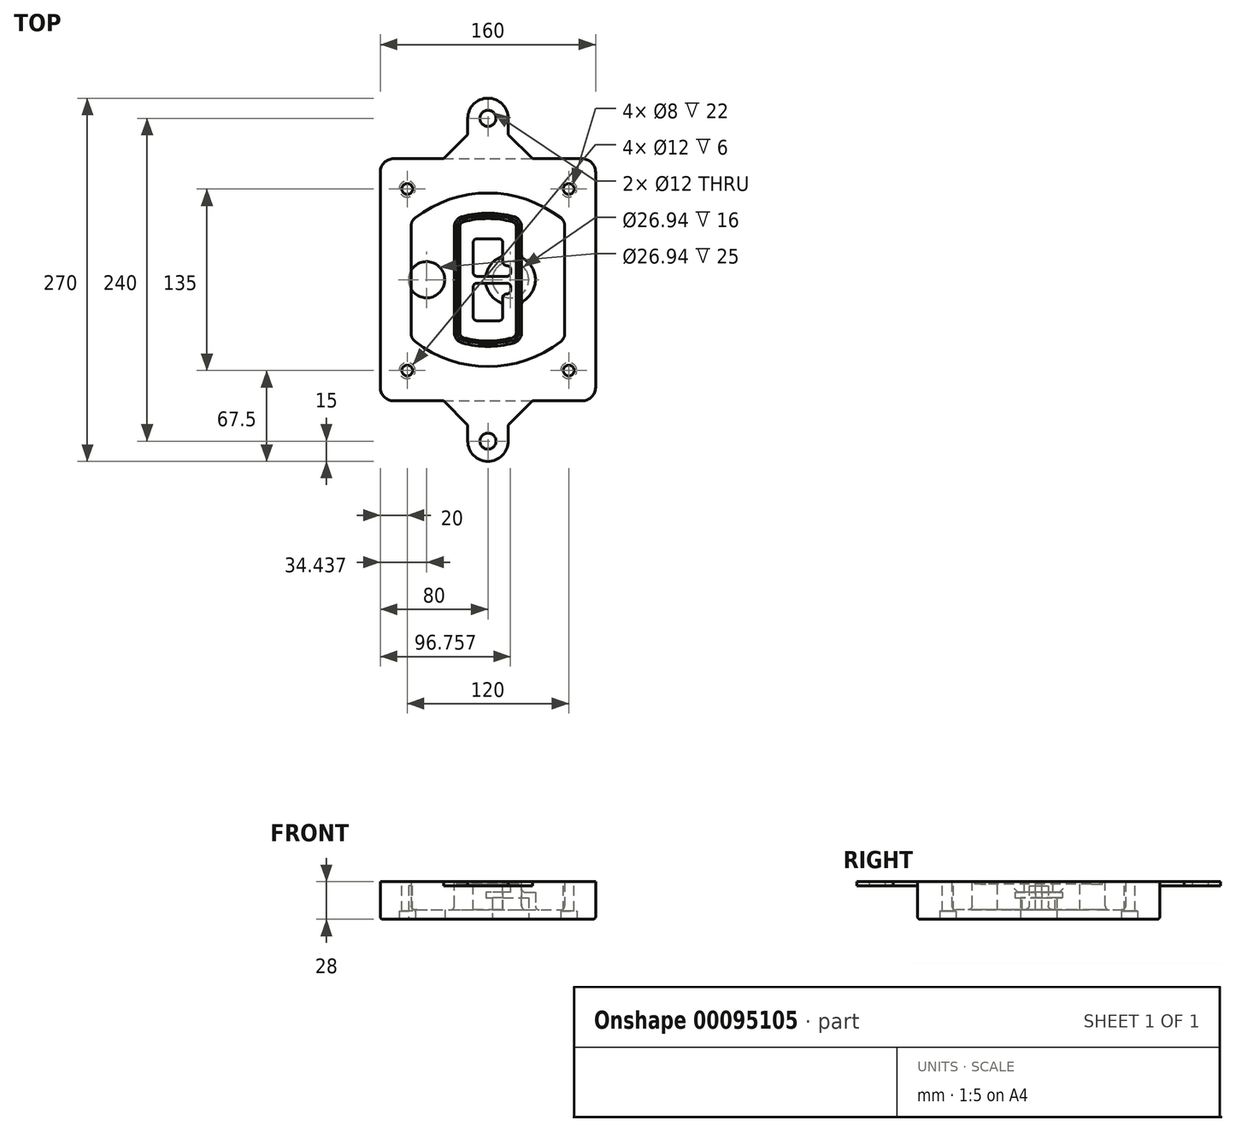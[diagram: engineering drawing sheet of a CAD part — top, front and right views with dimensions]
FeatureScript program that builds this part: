
annotation { "Feature Type Name" : "Feature", "Feature Type Description" : "" }
export const myFeature = defineFeature(function(context is Context, id is Id, definition is map)
    precondition{}
    {
        {
            var Q0;
            Q0=qCreatedBy(makeId("Top.planeOp"),FACE);
            var sketch = newSketch(context, id + "F0", { "sketchPlane" : qUnion([Q0])});
            skPoint(sketch, "E0.rect.middle", {"position": v(0, 0) * mm});
            skLineSegment(sketch, "E1.bottom", {"start": v(-70, -90) * mm, "end": v(70, -90) * mm});
            skLineSegment(sketch, "E1.top", {"start": v(-70, 90) * mm, "end": v(70, 90) * mm});
            skLineSegment(sketch, "E1.left", {"start": v(-80, -80) * mm, "end": v(-80, 80) * mm});
            skLineSegment(sketch, "E1.right", {"start": v(80, -80) * mm, "end": v(80, 80) * mm});
            skLineSegment(sketch, "E2", {"start": v(-80, 90) * mm, "end": v(80, -90) * mm, "construction": true});
            skLineSegment(sketch, "E3", {"start": v(80, 90) * mm, "end": v(-80, -90) * mm, "construction": true});
            skCircle(sketch, "E4", {"center": v(-60, 67.5) * mm, "radius": 4 * mm});
            skCircle(sketch, "E5", {"center": v(60, 67.5) * mm, "radius": 4 * mm});
            skCircle(sketch, "E6", {"center": v(60, -67.5) * mm, "radius": 4 * mm});
            skCircle(sketch, "E7", {"center": v(-60, -67.5) * mm, "radius": 4 * mm});
            skLineSegment(sketch, "E8", {"start": v(-60, 67.5) * mm, "end": v(60, 67.5) * mm, "construction": true});
            skLineSegment(sketch, "E9", {"start": v(60, 67.5) * mm, "end": v(60, -67.5) * mm, "construction": true});
            skLineSegment(sketch, "E10", {"start": v(60, -67.5) * mm, "end": v(-60, -67.5) * mm, "construction": true});
            skLineSegment(sketch, "E11", {"start": v(-60, -67.5) * mm, "end": v(-60, 67.5) * mm, "construction": true});
            skLineSegment(sketch, "E12", {"start": v(-60, 40.3) * mm, "end": v(-60, -40.3) * mm});
            skLineSegment(sketch, "E13", {"start": v(60, 40.3) * mm, "end": v(60, -40.3) * mm});
            skArc(sketch, "E14", {"start": v(56.15, 48.18) * mm, "mid": v(0, 67.5) * mm, "end": v(-56.15, 48.18) * mm});
            skArc(sketch, "E15", {"start": v(-56.15, -48.18) * mm, "mid": v(0, -67.5) * mm, "end": v(56.15, -48.18) * mm});
            skLineSegment(sketch, "E16", {"start": v(-60, 0) * mm, "end": v(60, 0) * mm, "construction": true});
            skPoint(sketch, "E17.visualSharp", {"position": v(-60, -45) * mm});
            skArc(sketch, "E17.filletArc", {"start": v(-60, -40.3) * mm, "mid": v(-58.99, -44.68) * mm, "end": v(-56.15, -48.18) * mm});
            skPoint(sketch, "E18.visualSharp", {"position": v(-60, 45) * mm});
            skArc(sketch, "E18.filletArc", {"start": v(-56.15, 48.18) * mm, "mid": v(-58.99, 44.68) * mm, "end": v(-60, 40.3) * mm});
            skPoint(sketch, "E19.visualSharp", {"position": v(60, 45) * mm});
            skArc(sketch, "E19.filletArc", {"start": v(60, 40.3) * mm, "mid": v(58.99, 44.68) * mm, "end": v(56.15, 48.18) * mm});
            skPoint(sketch, "E20.visualSharp", {"position": v(60, -45) * mm});
            skArc(sketch, "E20.filletArc", {"start": v(56.15, -48.18) * mm, "mid": v(58.99, -44.68) * mm, "end": v(60, -40.3) * mm});
            skPoint(sketch, "E21.visualSharp", {"position": v(-80, 90) * mm});
            skArc(sketch, "E21.filletArc", {"start": v(-70, 90) * mm, "mid": v(-77.07, 87.07) * mm, "end": v(-80, 80) * mm});
            skPoint(sketch, "E22.visualSharp", {"position": v(80, 90) * mm});
            skArc(sketch, "E22.filletArc", {"start": v(80, 80) * mm, "mid": v(77.07, 87.07) * mm, "end": v(70, 90) * mm});
            skPoint(sketch, "E23.visualSharp", {"position": v(80, -90) * mm});
            skArc(sketch, "E23.filletArc", {"start": v(70, -90) * mm, "mid": v(77.07, -87.07) * mm, "end": v(80, -80) * mm});
            skPoint(sketch, "E24.visualSharp", {"position": v(-80, -90) * mm});
            skArc(sketch, "E24.filletArc", {"start": v(-80, -80) * mm, "mid": v(-77.07, -87.07) * mm, "end": v(-70, -90) * mm});
            skArc(sketch, "E25.0", {"start": v(57, 40.3) * mm, "mid": v(56.3, 43.36) * mm, "end": v(54.3, 45.81) * mm});
            skLineSegment(sketch, "E25.1", {"start": v(57, 40.3) * mm, "end": v(57, -40.3) * mm});
            skArc(sketch, "E25.2", {"start": v(54.3, -45.81) * mm, "mid": v(56.3, -43.36) * mm, "end": v(57, -40.3) * mm});
            skArc(sketch, "E25.3", {"start": v(-54.3, -45.81) * mm, "mid": v(0, -64.5) * mm, "end": v(54.3, -45.81) * mm});
            skArc(sketch, "E25.4", {"start": v(-57, -40.3) * mm, "mid": v(-56.3, -43.36) * mm, "end": v(-54.3, -45.81) * mm});
            skArc(sketch, "E25.5", {"start": v(54.3, 45.81) * mm, "mid": v(0, 64.5) * mm, "end": v(-54.3, 45.81) * mm});
            skLineSegment(sketch, "E25.6", {"start": v(-57, 40.3) * mm, "end": v(-57, -40.3) * mm});
            skArc(sketch, "E25.7", {"start": v(-54.3, 45.81) * mm, "mid": v(-56.3, 43.36) * mm, "end": v(-57, 40.3) * mm});
            skArc(sketch, "E26.0", {"start": v(-58.62, 51.33) * mm, "mid": v(-62.58, 46.43) * mm, "end": v(-64, 40.3) * mm});
            skArc(sketch, "E26.1", {"start": v(58.62, 51.33) * mm, "mid": v(0, 71.5) * mm, "end": v(-58.62, 51.33) * mm});
            skArc(sketch, "E26.2", {"start": v(64, 40.3) * mm, "mid": v(62.58, 46.43) * mm, "end": v(58.62, 51.33) * mm});
            skLineSegment(sketch, "E26.3", {"start": v(64, 40.3) * mm, "end": v(64, -40.3) * mm});
            skArc(sketch, "E26.4", {"start": v(58.62, -51.33) * mm, "mid": v(62.58, -46.43) * mm, "end": v(64, -40.3) * mm});
            skLineSegment(sketch, "E26.5", {"start": v(-64, 40.3) * mm, "end": v(-64, -40.3) * mm});
            skArc(sketch, "E26.6", {"start": v(-58.62, -51.33) * mm, "mid": v(0, -71.5) * mm, "end": v(58.62, -51.33) * mm});
            skArc(sketch, "E26.7", {"start": v(-64, -40.3) * mm, "mid": v(-62.58, -46.43) * mm, "end": v(-58.62, -51.33) * mm});
            skSolve(sketch);
        }
        {
            var Q0;
            Q0=makeQuery(id+"F0.imprint","IMPRINT",FACE,{"disambiguationData":[TD([[makeQuery(id+"F0.imprint","IMPRINT",EDGE,{"derivedFrom":sQuery(id+"F0.wireOp",EDGE,"E1.bottom")}),1.0]])]});
            var Q1;
            Q1=makeQuery(id+"F0.imprint","IMPRINT",FACE,{"disambiguationData":[TD([[makeQuery(id+"F0.imprint","IMPRINT",EDGE,{"derivedFrom":sQuery(id+"F0.wireOp",EDGE,"E12")}),1.0]])]});
            var Q2;
            Q2=makeQuery(id+"F0.imprint","IMPRINT",FACE,{"disambiguationData":[TD([[makeQuery(id+"F0.imprint","IMPRINT",EDGE,{"derivedFrom":sQuery(id+"F0.wireOp",EDGE,"E25.0")}),1.0]])]});
            var Q3;
            Q3=makeQuery(id+"F0.imprint","IMPRINT",FACE,{"disambiguationData":[TD([[makeQuery(id+"F0.imprint","IMPRINT",EDGE,{"derivedFrom":sQuery(id+"F0.wireOp",EDGE,"E12")}),-1.0]])]});
            extrude(context, id + "F1", {"entities" : qUnion([Q0, Q1, Q2, Q3]), "oppositeDirection" : true, "depth" : 25 * mm});
        }
        {
            var Q0;
            Q0=makeQuery(id+"F0.imprint","IMPRINT",FACE,{"disambiguationData":[TD([[makeQuery(id+"F0.imprint","IMPRINT",EDGE,{"derivedFrom":sQuery(id+"F0.wireOp",EDGE,"E12")}),1.0]])]});
            extrude(context, id + "F2", {"entities" : qUnion([Q0]), "operationType" : NewBodyOperationType.ADD, "depth" : 3 * mm});
        }
        {
            var Q0;
            Q0=makeQuery(id+"F0.imprint","IMPRINT",FACE,{"disambiguationData":[TD([[makeQuery(id+"F0.imprint","IMPRINT",EDGE,{"derivedFrom":sQuery(id+"F0.wireOp",EDGE,"E25.0")}),1.0]])]});
            extrude(context, id + "F3", {"entities" : qUnion([Q0]), "operationType" : NewBodyOperationType.REMOVE, "oppositeDirection" : true, "depth" : 18 * mm});
        }
        {
            var Q0;
            Q0=makeQuery(id+"F2.opExtrude","CAP_FACE",FACE,{"disambiguationData":[OSD([sQuery(id+"F0.wireOp",EDGE,"E12"),sQuery(id+"F0.wireOp",EDGE,"E13"),sQuery(id+"F0.wireOp",EDGE,"E14"),sQuery(id+"F0.wireOp",EDGE,"E15"),sQuery(id+"F0.wireOp",EDGE,"E17.filletArc"),sQuery(id+"F0.wireOp",EDGE,"E18.filletArc"),sQuery(id+"F0.wireOp",EDGE,"E19.filletArc"),sQuery(id+"F0.wireOp",EDGE,"E20.filletArc"),sQuery(id+"F0.wireOp",EDGE,"E25.0"),sQuery(id+"F0.wireOp",EDGE,"E25.1"),sQuery(id+"F0.wireOp",EDGE,"E25.2"),sQuery(id+"F0.wireOp",EDGE,"E25.3"),sQuery(id+"F0.wireOp",EDGE,"E25.4"),sQuery(id+"F0.wireOp",EDGE,"E25.5"),sQuery(id+"F0.wireOp",EDGE,"E25.6"),sQuery(id+"F0.wireOp",EDGE,"E25.7")])],"isStart":false});
            var sketch = newSketch(context, id + "F4", { "sketchPlane" : qUnion([Q0])});
            skArc(sketch, "E27.0", {"start": v(-19.08, -46.97) * mm, "mid": v(0, -49.5) * mm, "end": v(19.08, -46.97) * mm});
            skArc(sketch, "E28.0", {"start": v(19.08, 46.97) * mm, "mid": v(0, 49.5) * mm, "end": v(-19.08, 46.97) * mm});
            skLineSegment(sketch, "E29", {"start": v(-25, 39.25) * mm, "end": v(-25, -39.25) * mm});
            skLineSegment(sketch, "E30", {"start": v(25, 39.25) * mm, "end": v(25, -39.25) * mm});
            skLineSegment(sketch, "E31", {"start": v(-25, 45.1) * mm, "end": v(25, 45.1) * mm, "construction": true});
            skLineSegment(sketch, "E32", {"start": v(-25, -45.1) * mm, "end": v(25, -45.1) * mm, "construction": true});
            skPoint(sketch, "E33.visualSharp", {"position": v(-25, 45.1) * mm});
            skArc(sketch, "E33.filletArc", {"start": v(-19.08, 46.97) * mm, "mid": v(-23.35, 44.11) * mm, "end": v(-25, 39.25) * mm});
            skPoint(sketch, "E34.visualSharp", {"position": v(25, 45.1) * mm});
            skArc(sketch, "E34.filletArc", {"start": v(25, 39.25) * mm, "mid": v(23.35, 44.11) * mm, "end": v(19.08, 46.97) * mm});
            skPoint(sketch, "E35.visualSharp", {"position": v(25, -45.1) * mm});
            skArc(sketch, "E35.filletArc", {"start": v(19.08, -46.97) * mm, "mid": v(23.35, -44.11) * mm, "end": v(25, -39.25) * mm});
            skPoint(sketch, "E36.visualSharp", {"position": v(-25, -45.1) * mm});
            skArc(sketch, "E36.filletArc", {"start": v(-25, -39.25) * mm, "mid": v(-23.35, -44.11) * mm, "end": v(-19.08, -46.97) * mm});
            skArc(sketch, "E37.0", {"start": v(54.3, 45.81) * mm, "mid": v(0, 64.5) * mm, "end": v(-54.3, 45.81) * mm});
            skArc(sketch, "E37.1", {"start": v(-54.3, 45.81) * mm, "mid": v(-56.3, 43.36) * mm, "end": v(-57, 40.3) * mm});
            skLineSegment(sketch, "E37.2", {"start": v(-57, 40.3) * mm, "end": v(-57, -40.3) * mm});
            skArc(sketch, "E37.3", {"start": v(-57, -40.3) * mm, "mid": v(-56.3, -43.36) * mm, "end": v(-54.3, -45.81) * mm});
            skArc(sketch, "E37.4", {"start": v(-54.3, -45.81) * mm, "mid": v(0, -64.5) * mm, "end": v(54.3, -45.81) * mm});
            skArc(sketch, "E37.5", {"start": v(54.3, -45.81) * mm, "mid": v(56.3, -43.36) * mm, "end": v(57, -40.3) * mm});
            skLineSegment(sketch, "E37.6", {"start": v(57, 40.3) * mm, "end": v(57, -40.3) * mm});
            skArc(sketch, "E37.7", {"start": v(57, 40.3) * mm, "mid": v(56.3, 43.36) * mm, "end": v(54.3, 45.81) * mm});
            skLineSegment(sketch, "E38.0", {"start": v(23, 39.25) * mm, "end": v(23, -39.25) * mm});
            skArc(sketch, "E38.1", {"start": v(18.56, -45.04) * mm, "mid": v(21.76, -42.9) * mm, "end": v(23, -39.25) * mm});
            skArc(sketch, "E38.2", {"start": v(-18.56, -45.04) * mm, "mid": v(0, -47.5) * mm, "end": v(18.56, -45.04) * mm});
            skArc(sketch, "E38.3", {"start": v(-23, -39.25) * mm, "mid": v(-21.76, -42.9) * mm, "end": v(-18.56, -45.04) * mm});
            skLineSegment(sketch, "E38.4", {"start": v(-23, 39.25) * mm, "end": v(-23, -39.25) * mm});
            skArc(sketch, "E38.5", {"start": v(23, 39.25) * mm, "mid": v(21.76, 42.9) * mm, "end": v(18.56, 45.04) * mm});
            skArc(sketch, "E38.6", {"start": v(-18.56, 45.04) * mm, "mid": v(-21.76, 42.9) * mm, "end": v(-23, 39.25) * mm});
            skArc(sketch, "E38.7", {"start": v(18.56, 45.04) * mm, "mid": v(0, 47.5) * mm, "end": v(-18.56, 45.04) * mm});
            skArc(sketch, "E39.0", {"start": v(21, 39.25) * mm, "mid": v(20.18, 41.68) * mm, "end": v(18.04, 43.1) * mm});
            skLineSegment(sketch, "E39.1", {"start": v(21, 39.25) * mm, "end": v(21, -39.25) * mm});
            skArc(sketch, "E39.2", {"start": v(18.04, -43.1) * mm, "mid": v(20.18, -41.68) * mm, "end": v(21, -39.25) * mm});
            skArc(sketch, "E39.3", {"start": v(-18.04, -43.1) * mm, "mid": v(0, -45.5) * mm, "end": v(18.04, -43.1) * mm});
            skArc(sketch, "E39.4", {"start": v(-21, -39.25) * mm, "mid": v(-20.18, -41.68) * mm, "end": v(-18.04, -43.1) * mm});
            skArc(sketch, "E39.5", {"start": v(18.04, 43.1) * mm, "mid": v(0, 45.5) * mm, "end": v(-18.04, 43.1) * mm});
            skLineSegment(sketch, "E39.6", {"start": v(-21, 39.25) * mm, "end": v(-21, -39.25) * mm});
            skArc(sketch, "E39.7", {"start": v(-18.04, 43.1) * mm, "mid": v(-20.18, 41.68) * mm, "end": v(-21, 39.25) * mm});
            skLineSegment(sketch, "E40", {"start": v(-25, 0) * mm, "end": v(25, 0) * mm, "construction": true});
            skLineSegment(sketch, "E41", {"start": v(-11, 5.5) * mm, "end": v(-11, 27.5) * mm});
            skLineSegment(sketch, "E42", {"start": v(-8, 30.5) * mm, "end": v(8, 30.5) * mm});
            skLineSegment(sketch, "E43", {"start": v(11, 27.5) * mm, "end": v(11, 13.5) * mm});
            skLineSegment(sketch, "E44", {"start": v(14, 10.5) * mm, "end": v(14, 10.5) * mm});
            skLineSegment(sketch, "E45", {"start": v(17, 7.5) * mm, "end": v(17, 5.5) * mm});
            skLineSegment(sketch, "E46", {"start": v(14, 2.5) * mm, "end": v(-8, 2.5) * mm});
            skPoint(sketch, "E47.visualSharp", {"position": v(-11, 30.5) * mm});
            skArc(sketch, "E47.filletArc", {"start": v(-8, 30.5) * mm, "mid": v(-10.12, 29.62) * mm, "end": v(-11, 27.5) * mm});
            skPoint(sketch, "E48.visualSharp", {"position": v(11, 30.5) * mm});
            skArc(sketch, "E48.filletArc", {"start": v(11, 27.5) * mm, "mid": v(10.12, 29.62) * mm, "end": v(8, 30.5) * mm});
            skPoint(sketch, "E49.visualSharp", {"position": v(11, 10.5) * mm});
            skArc(sketch, "E49.filletArc", {"start": v(11, 13.5) * mm, "mid": v(11.88, 11.38) * mm, "end": v(14, 10.5) * mm});
            skPoint(sketch, "E50.visualSharp", {"position": v(17, 10.5) * mm});
            skArc(sketch, "E50.filletArc", {"start": v(17, 7.5) * mm, "mid": v(16.12, 9.62) * mm, "end": v(14, 10.5) * mm});
            skPoint(sketch, "E51.visualSharp", {"position": v(17, 2.5) * mm});
            skArc(sketch, "E51.filletArc", {"start": v(14, 2.5) * mm, "mid": v(16.12, 3.38) * mm, "end": v(17, 5.5) * mm});
            skPoint(sketch, "E52.visualSharp", {"position": v(-11, 2.5) * mm});
            skArc(sketch, "E52.filletArc", {"start": v(-11, 5.5) * mm, "mid": v(-10.12, 3.38) * mm, "end": v(-8, 2.5) * mm});
            skLineSegment(sketch, "E53.0.MirrorCS", {"start": v(14, -2.5) * mm, "end": v(-8, -2.5) * mm});
            skArc(sketch, "E54.0.MirrorCS", {"start": v(-11, -5.5) * mm, "mid": v(-10.12, -3.38) * mm, "end": v(-8, -2.5) * mm});
            skLineSegment(sketch, "E55.0.MirrorCS", {"start": v(-11, -5.5) * mm, "end": v(-11, -27.5) * mm});
            skArc(sketch, "E56.0.MirrorCS", {"start": v(-8, -30.5) * mm, "mid": v(-10.12, -29.62) * mm, "end": v(-11, -27.5) * mm});
            skLineSegment(sketch, "E57.0.MirrorCS", {"start": v(-8, -30.5) * mm, "end": v(8, -30.5) * mm});
            skArc(sketch, "E58.0.MirrorCS", {"start": v(11, -27.5) * mm, "mid": v(10.12, -29.62) * mm, "end": v(8, -30.5) * mm});
            skLineSegment(sketch, "E59.0.MirrorCS", {"start": v(11, -27.5) * mm, "end": v(11, -13.5) * mm});
            skArc(sketch, "E60.0.MirrorCS", {"start": v(11, -13.5) * mm, "mid": v(11.88, -11.38) * mm, "end": v(14, -10.5) * mm});
            skArc(sketch, "E61.0.MirrorCS", {"start": v(17, -7.5) * mm, "mid": v(16.12, -9.62) * mm, "end": v(14, -10.5) * mm});
            skLineSegment(sketch, "E62.0.MirrorCS", {"start": v(17, -7.5) * mm, "end": v(17, -5.5) * mm});
            skArc(sketch, "E63.0.MirrorCS", {"start": v(14, -2.5) * mm, "mid": v(16.12, -3.38) * mm, "end": v(17, -5.5) * mm});
            skSolve(sketch);
        }
        {
            var Q0;
            Q0=makeQuery(id+"F4.imprint","IMPRINT",FACE,{"disambiguationData":[TD([[makeQuery(id+"F4.imprint","IMPRINT",EDGE,{"derivedFrom":sQuery(id+"F4.wireOp",EDGE,"E27.0")}),1.0]])]});
            var Q1;
            Q1=makeQuery(id+"F4.imprint","IMPRINT",FACE,{"disambiguationData":[TD([[makeQuery(id+"F4.imprint","IMPRINT",EDGE,{"derivedFrom":sQuery(id+"F4.wireOp",EDGE,"E38.0")}),-1.0]])]});
            var Q2;
            Q2=makeQuery(id+"F4.imprint","IMPRINT",FACE,{"disambiguationData":[TD([[makeQuery(id+"F4.imprint","IMPRINT",EDGE,{"derivedFrom":sQuery(id+"F4.wireOp",EDGE,"E39.0")}),1.0]])]});
            extrude(context, id + "F5", {"entities" : qUnion([Q0, Q1, Q2]), "operationType" : NewBodyOperationType.ADD, "endBound" : BoundingType.UP_TO_NEXT, "oppositeDirection" : true, "depth" : 25 * mm});
        }
        {
            var Q0;
            Q0=makeQuery(id+"F4.imprint","IMPRINT",FACE,{"disambiguationData":[TD([[makeQuery(id+"F4.imprint","IMPRINT",EDGE,{"derivedFrom":sQuery(id+"F4.wireOp",EDGE,"E38.0")}),-1.0]])]});
            extrude(context, id + "F6", {"entities" : qUnion([Q0]), "operationType" : NewBodyOperationType.REMOVE, "oppositeDirection" : true, "depth" : 2 * mm});
        }
        {
            var Q0;
            Q0=makeQuery(id+"F1.opExtrude","CAP_FACE",FACE,{"disambiguationData":[OSD([sQuery(id+"F0.wireOp",EDGE,"E1.bottom"),sQuery(id+"F0.wireOp",EDGE,"E1.top"),sQuery(id+"F0.wireOp",EDGE,"E1.left"),sQuery(id+"F0.wireOp",EDGE,"E1.right"),sQuery(id+"F0.wireOp",EDGE,"E4"),sQuery(id+"F0.wireOp",EDGE,"E5"),sQuery(id+"F0.wireOp",EDGE,"E6"),sQuery(id+"F0.wireOp",EDGE,"E7"),sQuery(id+"F0.wireOp",EDGE,"E21.filletArc"),sQuery(id+"F0.wireOp",EDGE,"E22.filletArc"),sQuery(id+"F0.wireOp",EDGE,"E23.filletArc"),sQuery(id+"F0.wireOp",EDGE,"E24.filletArc")])],"isStart":false});
            var sketch = newSketch(context, id + "F7", { "sketchPlane" : qUnion([Q0])});
            skCircle(sketch, "E64", {"center": v(16.76, 0) * mm, "radius": 13.47 * mm});
            skCircle(sketch, "E65", {"center": v(-45.56, 0) * mm, "radius": 13.47 * mm});
            skLineSegment(sketch, "E66", {"start": v(80, 0) * mm, "end": v(-80, 0) * mm});
            skCircle(sketch, "E67", {"center": v(16.76, 0) * mm, "radius": 18.47 * mm});
            skCircle(sketch, "E68", {"center": v(60, -67.5) * mm, "radius": 6 * mm});
            skCircle(sketch, "E69", {"center": v(-60, -67.5) * mm, "radius": 6 * mm});
            skCircle(sketch, "E70", {"center": v(-60, 67.5) * mm, "radius": 6 * mm});
            skCircle(sketch, "E71", {"center": v(60, 67.5) * mm, "radius": 6 * mm});
            skSolve(sketch);
        }
        {
            var Q0;
            {var subQ1=sQuery(id+"F7.wireOp",EDGE,"E66");var subQ4=sQuery(id+"F7.wireOp",EDGE,"E64");var subQ6=makeQuery(id+"F7.imprint","INTERSECT",VERTEX,{"disambiguationData":[OD(0.0)],"derivedFrom":[subQ4,subQ1]});Q0=makeQuery(id+"F7.imprint","IMPRINT",FACE,{"disambiguationData":[TD([[makeQuery(id+"F7.imprint","IMPRINT",EDGE,{"disambiguationData":[TD([[subQ6,-1.0]])],"derivedFrom":subQ4}),-1.0]])]});}
            var Q1;
            {var subQ0=sQuery(id+"F7.wireOp",EDGE,"E66");var subQ1=sQuery(id+"F7.wireOp",EDGE,"E64");var subQ3=makeQuery(id+"F7.imprint","INTERSECT",VERTEX,{"disambiguationData":[OD(0.0)],"derivedFrom":[subQ1,subQ0]});Q1=makeQuery(id+"F7.imprint","IMPRINT",FACE,{"disambiguationData":[TD([[makeQuery(id+"F7.imprint","IMPRINT",EDGE,{"disambiguationData":[TD([[subQ3,-1.0]])],"derivedFrom":subQ1}),1.0]])]});}
            var Q2;
            {var subQ0=sQuery(id+"F7.wireOp",EDGE,"E66");var subQ1=sQuery(id+"F7.wireOp",EDGE,"E64");var subQ3=makeQuery(id+"F7.imprint","INTERSECT",VERTEX,{"disambiguationData":[OD(0.0)],"derivedFrom":[subQ1,subQ0]});Q2=makeQuery(id+"F7.imprint","IMPRINT",FACE,{"disambiguationData":[TD([[makeQuery(id+"F7.imprint","IMPRINT",EDGE,{"disambiguationData":[TD([[subQ3,1.0]])],"derivedFrom":subQ1}),1.0]])]});}
            var Q3;
            {var subQ1=sQuery(id+"F7.wireOp",EDGE,"E66");var subQ4=sQuery(id+"F7.wireOp",EDGE,"E64");var subQ6=makeQuery(id+"F7.imprint","INTERSECT",VERTEX,{"disambiguationData":[OD(0.0)],"derivedFrom":[subQ4,subQ1]});Q3=makeQuery(id+"F7.imprint","IMPRINT",FACE,{"disambiguationData":[TD([[makeQuery(id+"F7.imprint","IMPRINT",EDGE,{"disambiguationData":[TD([[subQ6,1.0]])],"derivedFrom":subQ4}),-1.0]])]});}
            extrude(context, id + "F8", {"entities" : qUnion([Q0, Q1, Q2, Q3]), "operationType" : NewBodyOperationType.ADD, "oppositeDirection" : true, "depth" : 20 * mm});
        }
        {
            var Q0;
            {var subQ0=sQuery(id+"F7.wireOp",EDGE,"E66");var subQ1=sQuery(id+"F7.wireOp",EDGE,"E64");var subQ3=makeQuery(id+"F7.imprint","INTERSECT",VERTEX,{"disambiguationData":[OD(0.0)],"derivedFrom":[subQ1,subQ0]});Q0=makeQuery(id+"F7.imprint","IMPRINT",FACE,{"disambiguationData":[TD([[makeQuery(id+"F7.imprint","IMPRINT",EDGE,{"disambiguationData":[TD([[subQ3,-1.0]])],"derivedFrom":subQ1}),1.0]])]});}
            var Q1;
            {var subQ0=sQuery(id+"F7.wireOp",EDGE,"E66");var subQ1=sQuery(id+"F7.wireOp",EDGE,"E64");var subQ3=makeQuery(id+"F7.imprint","INTERSECT",VERTEX,{"disambiguationData":[OD(0.0)],"derivedFrom":[subQ1,subQ0]});Q1=makeQuery(id+"F7.imprint","IMPRINT",FACE,{"disambiguationData":[TD([[makeQuery(id+"F7.imprint","IMPRINT",EDGE,{"disambiguationData":[TD([[subQ3,1.0]])],"derivedFrom":subQ1}),1.0]])]});}
            extrude(context, id + "F9", {"entities" : qUnion([Q0, Q1]), "operationType" : NewBodyOperationType.REMOVE, "oppositeDirection" : true, "depth" : 16 * mm});
        }
        {
            var Q0;
            {var subQ0=sQuery(id+"F7.wireOp",EDGE,"E66");var subQ1=sQuery(id+"F7.wireOp",EDGE,"E65");var subQ3=makeQuery(id+"F7.imprint","INTERSECT",VERTEX,{"disambiguationData":[OD(0.0)],"derivedFrom":[subQ1,subQ0]});Q0=makeQuery(id+"F7.imprint","IMPRINT",FACE,{"disambiguationData":[TD([[makeQuery(id+"F7.imprint","IMPRINT",EDGE,{"disambiguationData":[TD([[subQ3,-1.0]])],"derivedFrom":subQ1}),1.0]])]});}
            var Q1;
            {var subQ0=sQuery(id+"F7.wireOp",EDGE,"E66");var subQ1=sQuery(id+"F7.wireOp",EDGE,"E65");var subQ3=makeQuery(id+"F7.imprint","INTERSECT",VERTEX,{"disambiguationData":[OD(0.0)],"derivedFrom":[subQ1,subQ0]});Q1=makeQuery(id+"F7.imprint","IMPRINT",FACE,{"disambiguationData":[TD([[makeQuery(id+"F7.imprint","IMPRINT",EDGE,{"disambiguationData":[TD([[subQ3,1.0]])],"derivedFrom":subQ1}),1.0]])]});}
            extrude(context, id + "F10", {"entities" : qUnion([Q0, Q1]), "operationType" : NewBodyOperationType.REMOVE, "oppositeDirection" : true, "depth" : 25 * mm});
        }
        {
            var Q0;
            Q0=makeQuery(id+"F7.imprint","IMPRINT",FACE,{"disambiguationData":[TD([[makeQuery(id+"F7.imprint","IMPRINT",EDGE,{"derivedFrom":sQuery(id+"F7.wireOp",EDGE,"E68")}),1.0]])]});
            var Q1;
            Q1=makeQuery(id+"F7.imprint","IMPRINT",FACE,{"disambiguationData":[TD([[makeQuery(id+"F7.imprint","IMPRINT",EDGE,{"derivedFrom":makeQuery(id+"F1.opExtrude","CAP_EDGE",EDGE,{"disambiguationData":[OSD([sQuery(id+"F0.wireOp",EDGE,"E5")])],"isStart":false})}),-1.0]])]});
            var Q2;
            Q2=makeQuery(id+"F7.imprint","IMPRINT",FACE,{"disambiguationData":[TD([[makeQuery(id+"F7.imprint","IMPRINT",EDGE,{"derivedFrom":sQuery(id+"F7.wireOp",EDGE,"E69")}),1.0]])]});
            var Q3;
            Q3=makeQuery(id+"F7.imprint","IMPRINT",FACE,{"disambiguationData":[TD([[makeQuery(id+"F7.imprint","IMPRINT",EDGE,{"derivedFrom":makeQuery(id+"F1.opExtrude","CAP_EDGE",EDGE,{"disambiguationData":[OSD([sQuery(id+"F0.wireOp",EDGE,"E4")])],"isStart":false})}),-1.0]])]});
            var Q4;
            Q4=makeQuery(id+"F7.imprint","IMPRINT",FACE,{"disambiguationData":[TD([[makeQuery(id+"F7.imprint","IMPRINT",EDGE,{"derivedFrom":sQuery(id+"F7.wireOp",EDGE,"E70")}),1.0]])]});
            var Q5;
            Q5=makeQuery(id+"F7.imprint","IMPRINT",FACE,{"disambiguationData":[TD([[makeQuery(id+"F7.imprint","IMPRINT",EDGE,{"derivedFrom":makeQuery(id+"F1.opExtrude","CAP_EDGE",EDGE,{"disambiguationData":[OSD([sQuery(id+"F0.wireOp",EDGE,"E7")])],"isStart":false})}),-1.0]])]});
            var Q6;
            Q6=makeQuery(id+"F7.imprint","IMPRINT",FACE,{"disambiguationData":[TD([[makeQuery(id+"F7.imprint","IMPRINT",EDGE,{"derivedFrom":sQuery(id+"F7.wireOp",EDGE,"E71")}),1.0]])]});
            var Q7;
            Q7=makeQuery(id+"F7.imprint","IMPRINT",FACE,{"disambiguationData":[TD([[makeQuery(id+"F7.imprint","IMPRINT",EDGE,{"derivedFrom":makeQuery(id+"F1.opExtrude","CAP_EDGE",EDGE,{"disambiguationData":[OSD([sQuery(id+"F0.wireOp",EDGE,"E6")])],"isStart":false})}),-1.0]])]});
            extrude(context, id + "F11", {"entities" : qUnion([Q0, Q1, Q2, Q3, Q4, Q5, Q6, Q7]), "operationType" : NewBodyOperationType.REMOVE, "oppositeDirection" : true, "depth" : 6 * mm});
        }
        {
            var Q0;
            Q0=makeQuery(id+"F9.boolean.opBoolean","COPY",FACE,{"derivedFrom":makeQuery(id+"F9.opExtrude","CAP_FACE",FACE,{"disambiguationData":[OSD([sQuery(id+"F7.wireOp",EDGE,"E64")])],"isStart":false})});
            var sketch = newSketch(context, id + "F12", { "sketchPlane" : qUnion([Q0])});
            skArc(sketch, "E72.0", {"start": v(11, 17.55) * mm, "mid": v(2.57, 11.82) * mm, "end": v(-1.54, 2.5) * mm});
            skArc(sketch, "E72.1", {"start": v(-1.54, -2.5) * mm, "mid": v(2.57, -11.82) * mm, "end": v(11, -17.55) * mm});
            skLineSegment(sketch, "E73", {"start": v(-1.54, -2.5) * mm, "end": v(14, -2.5) * mm});
            skLineSegment(sketch, "E74.0", {"start": v(14, 2.5) * mm, "end": v(-1.54, 2.5) * mm});
            skArc(sketch, "E74.1", {"start": v(14, 2.5) * mm, "mid": v(16.12, 3.38) * mm, "end": v(17, 5.5) * mm});
            skLineSegment(sketch, "E74.2", {"start": v(17, 7.5) * mm, "end": v(17, 5.5) * mm});
            skArc(sketch, "E74.3", {"start": v(17, 7.5) * mm, "mid": v(16.12, 9.62) * mm, "end": v(14, 10.5) * mm});
            skArc(sketch, "E74.4", {"start": v(11, 13.5) * mm, "mid": v(11.88, 11.38) * mm, "end": v(14, 10.5) * mm});
            skLineSegment(sketch, "E74.5", {"start": v(11, 17.55) * mm, "end": v(11, 13.5) * mm});
            skLineSegment(sketch, "E74.7", {"start": v(14, -2.5) * mm, "end": v(-1.54, -2.5) * mm});
            skArc(sketch, "E74.8", {"start": v(14, -2.5) * mm, "mid": v(16.12, -3.38) * mm, "end": v(17, -5.5) * mm});
            skLineSegment(sketch, "E74.9", {"start": v(17, -7.5) * mm, "end": v(17, -5.5) * mm});
            skArc(sketch, "E74.10", {"start": v(17, -7.5) * mm, "mid": v(16.12, -9.62) * mm, "end": v(14, -10.5) * mm});
            skArc(sketch, "E74.11", {"start": v(11, -13.5) * mm, "mid": v(11.88, -11.38) * mm, "end": v(14, -10.5) * mm});
            skLineSegment(sketch, "E74.12", {"start": v(11, -17.55) * mm, "end": v(11, -13.5) * mm});
            skPoint(sketch, "E75.orphan", {"position": v(11, -27.5) * mm});
            skPoint(sketch, "E76.orphan", {"position": v(-8, -2.5) * mm});
            skPoint(sketch, "E77.orphan", {"position": v(-8, 2.5) * mm});
            skPoint(sketch, "E78.orphan", {"position": v(11, 27.5) * mm});
            skSolve(sketch);
        }
        {
            var Q0;
            {var subQ7=sQuery(id+"F12.wireOp",EDGE,"E72.0");var subQ14=sQuery(id+"F12.wireOp",EDGE,"E72.1");var subQ16=sQuery(id+"F12.wireOp",EDGE,"E74.1");var subQ18=sQuery(id+"F12.wireOp",EDGE,"E74.8");Q0=qUnion([makeQuery(id+"F12.imprint","IMPRINT",FACE,{"disambiguationData":[TD([[makeQuery(id+"F12.imprint","IMPRINT",EDGE,{"derivedFrom":subQ7}),1.0]])]}),makeQuery(id+"F12.imprint","IMPRINT",FACE,{"disambiguationData":[TD([[makeQuery(id+"F12.imprint","IMPRINT",EDGE,{"derivedFrom":subQ14}),1.0]])]}),makeQuery(id+"F12.imprint","IMPRINT",FACE,{"disambiguationData":[TD([[makeQuery(id+"F12.imprint","IMPRINT",EDGE,{"derivedFrom":subQ16}),1.0]])]}),makeQuery(id+"F12.imprint","IMPRINT",FACE,{"disambiguationData":[TD([[makeQuery(id+"F12.imprint","IMPRINT",EDGE,{"derivedFrom":subQ18}),-1.0]])]})]);}
            var Q1;
            Q1=makeQuery(id+"F5.boolean.opBoolean","SPLIT",FACE,{"disambiguationData":[TD([makeQuery(id+"F5.opExtrude","SWEPT_FACE",FACE,{"disambiguationData":[OSD([sQuery(id+"F4.wireOp",EDGE,"E41")])]})])],"derivedFrom":makeQuery(id+"F3.boolean.opBoolean","COPY",FACE,{"derivedFrom":makeQuery(id+"F3.opExtrude","CAP_FACE",FACE,{"disambiguationData":[OSD([sQuery(id+"F0.wireOp",EDGE,"E25.0"),sQuery(id+"F0.wireOp",EDGE,"E25.1"),sQuery(id+"F0.wireOp",EDGE,"E25.2"),sQuery(id+"F0.wireOp",EDGE,"E25.3"),sQuery(id+"F0.wireOp",EDGE,"E25.4"),sQuery(id+"F0.wireOp",EDGE,"E25.5"),sQuery(id+"F0.wireOp",EDGE,"E25.6"),sQuery(id+"F0.wireOp",EDGE,"E25.7")])],"isStart":false})})});
            extrude(context, id + "F13", {"entities" : qUnion([Q0]), "operationType" : NewBodyOperationType.REMOVE, "endBound" : BoundingType.UP_TO_SURFACE, "endBoundEntityFace" : qUnion([Q1]), "depth" : 25 * mm});
        }
        {
            var Q0;
            Q0=makeQuery(id+"F3.boolean.opBoolean","COPY",EDGE,{"derivedFrom":makeQuery(id+"F3.opExtrude","CAP_EDGE",EDGE,{"disambiguationData":[OSD([sQuery(id+"F0.wireOp",EDGE,"E25.6")])],"isStart":false})});
            var Q1;
            Q1=makeQuery(id+"F8.boolean.opBoolean","INTERSECT",EDGE,{"derivedFrom":[makeQuery(id+"F5.opExtrude","SWEPT_FACE",FACE,{"disambiguationData":[OSD([sQuery(id+"F4.wireOp",EDGE,"E30")])]}),makeQuery(id+"F8.opExtrude","CAP_FACE",FACE,{"disambiguationData":[OSD([sQuery(id+"F7.wireOp",EDGE,"E67")])],"isStart":false})]});
            var Q2;
            Q2=makeQuery(id+"F8.boolean.opBoolean","INTERSECT",EDGE,{"disambiguationData":[OD(1.0)],"derivedFrom":[makeQuery(id+"F5.opExtrude","SWEPT_FACE",FACE,{"disambiguationData":[OSD([sQuery(id+"F4.wireOp",EDGE,"E30")])]}),makeQuery(id+"F8.opExtrude","SWEPT_FACE",FACE,{"disambiguationData":[OSD([sQuery(id+"F7.wireOp",EDGE,"E67")])]})]});
            var Q3;
            {var subQ0=sQuery(id+"F4.wireOp",EDGE,"E30");Q3=makeQuery(id+"F8.boolean.opBoolean","SPLIT",EDGE,{"disambiguationData":[TD([makeQuery(id+"F5.opExtrude","SWEPT_FACE",FACE,{"disambiguationData":[OSD([sQuery(id+"F4.wireOp",EDGE,"E35.filletArc")])]})])],"derivedFrom":makeQuery(id+"F5.opExtrude","CAP_EDGE",EDGE,{"disambiguationData":[OSD([subQ0])],"isStart":false})});}
            var Q4;
            {var subQ0=sQuery(id+"F0.wireOp",EDGE,"E25.7");var subQ1=sQuery(id+"F0.wireOp",EDGE,"E25.1");var subQ2=sQuery(id+"F0.wireOp",EDGE,"E25.6");var subQ3=sQuery(id+"F0.wireOp",EDGE,"E25.5");var subQ4=sQuery(id+"F0.wireOp",EDGE,"E25.4");var subQ5=sQuery(id+"F0.wireOp",EDGE,"E25.0");var subQ6=sQuery(id+"F0.wireOp",EDGE,"E25.2");var subQ7=sQuery(id+"F0.wireOp",EDGE,"E25.3");Q4=makeQuery(id+"F8.boolean.opBoolean","INTERSECT",EDGE,{"derivedFrom":[makeQuery(id+"F5.boolean.opBoolean","SPLIT",FACE,{"disambiguationData":[TD([makeQuery(id+"F2.opExtrude","SWEPT_FACE",FACE,{"disambiguationData":[OSD([subQ5])]})])],"derivedFrom":makeQuery(id+"F3.boolean.opBoolean","COPY",FACE,{"derivedFrom":makeQuery(id+"F3.opExtrude","CAP_FACE",FACE,{"disambiguationData":[OSD([subQ5,subQ1,subQ6,subQ7,subQ4,subQ3,subQ2,subQ0])],"isStart":false})})}),makeQuery(id+"F8.opExtrude","SWEPT_FACE",FACE,{"disambiguationData":[OSD([sQuery(id+"F7.wireOp",EDGE,"E67")])]})]});}
            var Q5;
            Q5=makeQuery(id+"F8.boolean.opBoolean","INTERSECT",EDGE,{"disambiguationData":[OD(0.0)],"derivedFrom":[makeQuery(id+"F5.opExtrude","SWEPT_FACE",FACE,{"disambiguationData":[OSD([sQuery(id+"F4.wireOp",EDGE,"E30")])]}),makeQuery(id+"F8.opExtrude","SWEPT_FACE",FACE,{"disambiguationData":[OSD([sQuery(id+"F7.wireOp",EDGE,"E67")])]})]});
            fillet(context, id + "F14", {"entities" : qUnion([Q0, Q1, Q2, Q3, Q4, Q5]), "radius" : 3 * mm, "tangentPropagation" : true, "allowEdgeOverflow" : false});
        }
        {
            var Q0;
            Q0=makeQuery(id+"F1.opExtrude","CAP_EDGE",EDGE,{"disambiguationData":[OSD([sQuery(id+"F0.wireOp",EDGE,"E1.bottom")])],"isStart":false});
            fillet(context, id + "F15", {"entities" : qUnion([Q0]), "radius" : 2 * mm, "tangentPropagation" : true, "allowEdgeOverflow" : false});
        }
        {
            var Q0;
            {var subQ0=sQuery(id+"F0.wireOp",EDGE,"E22.filletArc");var subQ1=sQuery(id+"F0.wireOp",EDGE,"E7");var subQ2=sQuery(id+"F0.wireOp",EDGE,"E6");var subQ3=sQuery(id+"F0.wireOp",EDGE,"E5");var subQ4=sQuery(id+"F0.wireOp",EDGE,"E4");var subQ5=sQuery(id+"F0.wireOp",EDGE,"E1.bottom");var subQ6=sQuery(id+"F0.wireOp",EDGE,"E21.filletArc");var subQ7=sQuery(id+"F0.wireOp",EDGE,"E1.top");var subQ8=sQuery(id+"F0.wireOp",EDGE,"E1.left");var subQ9=sQuery(id+"F0.wireOp",EDGE,"E1.right");var subQ10=sQuery(id+"F0.wireOp",EDGE,"E23.filletArc");var subQ11=sQuery(id+"F0.wireOp",EDGE,"E24.filletArc");Q0=makeQuery(id+"F2.boolean.opBoolean","SPLIT",FACE,{"disambiguationData":[TD([makeQuery(id+"F1.opExtrude","SWEPT_FACE",FACE,{"disambiguationData":[OSD([subQ5])]})])],"derivedFrom":makeQuery(id+"F1.opExtrude","CAP_FACE",FACE,{"disambiguationData":[OSD([subQ5,subQ7,subQ8,subQ9,subQ4,subQ3,subQ2,subQ1,subQ6,subQ0,subQ10,subQ11])],"isStart":true})});}
            var sketch = newSketch(context, id + "F16", { "sketchPlane" : qUnion([Q0])});
            skLineSegment(sketch, "E79", {"start": v(-33, 90) * mm, "end": v(-15, 108) * mm});
            skLineSegment(sketch, "E80", {"start": v(-15, 108) * mm, "end": v(-15, 120) * mm});
            skLineSegment(sketch, "E81", {"start": v(0, 90) * mm, "end": v(0, 120) * mm, "construction": true});
            skArc(sketch, "E82", {"start": v(-15, 120) * mm, "mid": v(0, 135) * mm, "end": v(15, 120) * mm});
            skLineSegment(sketch, "E83", {"start": v(15, 120) * mm, "end": v(15, 108) * mm});
            skLineSegment(sketch, "E84", {"start": v(15, 108) * mm, "end": v(33, 90) * mm});
            skCircle(sketch, "E85", {"center": v(0, 120) * mm, "radius": 6 * mm});
            skLineSegment(sketch, "E86", {"start": v(-80, 0) * mm, "end": v(80, 0) * mm, "construction": true});
            skLineSegment(sketch, "E87.MirrorCS", {"start": v(-33, -90) * mm, "end": v(-15, -108) * mm});
            skLineSegment(sketch, "E88.MirrorCS", {"start": v(15, -108) * mm, "end": v(33, -90) * mm});
            skLineSegment(sketch, "E89.MirrorCS", {"start": v(0, -90) * mm, "end": v(0, -120) * mm, "construction": true});
            skLineSegment(sketch, "E90.MirrorCS", {"start": v(15, -120) * mm, "end": v(15, -108) * mm});
            skArc(sketch, "E91.MirrorCS", {"start": v(-15, -120) * mm, "mid": v(0, -135) * mm, "end": v(15, -120) * mm});
            skCircle(sketch, "E92.MirrorC", {"center": v(0, -120) * mm, "radius": 6 * mm});
            skLineSegment(sketch, "E93.MirrorCS", {"start": v(-15, -108) * mm, "end": v(-15, -120) * mm});
            skSolve(sketch);
        }
        {
            var Q0;
            Q0=makeQuery(id+"F16.imprint","IMPRINT",FACE,{"disambiguationData":[TD([[makeQuery(id+"F16.imprint","IMPRINT",EDGE,{"derivedFrom":makeQuery(id+"F1.opExtrude","CAP_EDGE",EDGE,{"disambiguationData":[OSD([sQuery(id+"F0.wireOp",EDGE,"E1.left")])],"isStart":true})}),-1.0]])]});
            var Q1;
            {var subQ0=sQuery(id+"F16.wireOp",EDGE,"E87.MirrorCS");Q1=makeQuery(id+"F16.imprint","IMPRINT",FACE,{"disambiguationData":[TD([[makeQuery(id+"F16.imprint","IMPRINT",EDGE,{"derivedFrom":subQ0}),1.0]])]});}
            var Q2;
            {var subQ0=sQuery(id+"F16.wireOp",EDGE,"E79");Q2=makeQuery(id+"F16.imprint","IMPRINT",FACE,{"disambiguationData":[TD([[makeQuery(id+"F16.imprint","IMPRINT",EDGE,{"derivedFrom":subQ0}),-1.0]])]});}
            var Q3;
            Q3=makeQuery(id+"F2.opExtrude","CAP_FACE",FACE,{"disambiguationData":[OSD([sQuery(id+"F0.wireOp",EDGE,"E12"),sQuery(id+"F0.wireOp",EDGE,"E13"),sQuery(id+"F0.wireOp",EDGE,"E14"),sQuery(id+"F0.wireOp",EDGE,"E15"),sQuery(id+"F0.wireOp",EDGE,"E17.filletArc"),sQuery(id+"F0.wireOp",EDGE,"E18.filletArc"),sQuery(id+"F0.wireOp",EDGE,"E19.filletArc"),sQuery(id+"F0.wireOp",EDGE,"E20.filletArc"),sQuery(id+"F0.wireOp",EDGE,"E25.0"),sQuery(id+"F0.wireOp",EDGE,"E25.1"),sQuery(id+"F0.wireOp",EDGE,"E25.2"),sQuery(id+"F0.wireOp",EDGE,"E25.3"),sQuery(id+"F0.wireOp",EDGE,"E25.4"),sQuery(id+"F0.wireOp",EDGE,"E25.5"),sQuery(id+"F0.wireOp",EDGE,"E25.6"),sQuery(id+"F0.wireOp",EDGE,"E25.7")])],"isStart":false});
            extrude(context, id + "F17", {"entities" : qUnion([Q0, Q1, Q2]), "operationType" : NewBodyOperationType.ADD, "endBound" : BoundingType.UP_TO_SURFACE, "endBoundEntityFace" : qUnion([Q3]), "depth" : 25 * mm});
        }
    });
